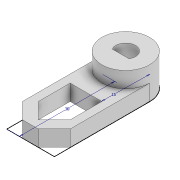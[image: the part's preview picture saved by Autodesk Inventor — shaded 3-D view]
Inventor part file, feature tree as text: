
AUTODESK INVENTOR PART (.ipt)
format: ipt  version: 2020.3 (Build 243373000, 373)  size: 108,544 bytes
history: native  units: mm
features: extrude x3, sketch x2, chamfer x1
ambient origin geometry x8: Origin, YZ Plane, XZ Plane, XY Plane, X Axis, Y Axis, Z Axis, Center Point
bodies: Solid1 (feature_tree)
feature tree (6):
  sketch  "Sketch1"  dims[d1=15.0mm d2=30.0mm]
  extrude  "Extrusion1"  Depth=15.0mm
  extrude  "Extrusion2"  Depth=5.0mm TaperAngle=0.0deg
  chamfer  "Chamfer1"  Distance=5.0mm Angle=45.0deg
  extrude  "Extrusion3"  Depth=5.0mm TaperAngle=0.0deg
  sketch  "Sketch3"  dims[d3=10.0mm d4=0.0mm d5=5.0mm d6=0.0mm d7=5.0mm d8=2.0mm d9=45.0deg d10=5.5mm d11=0.0mm]
